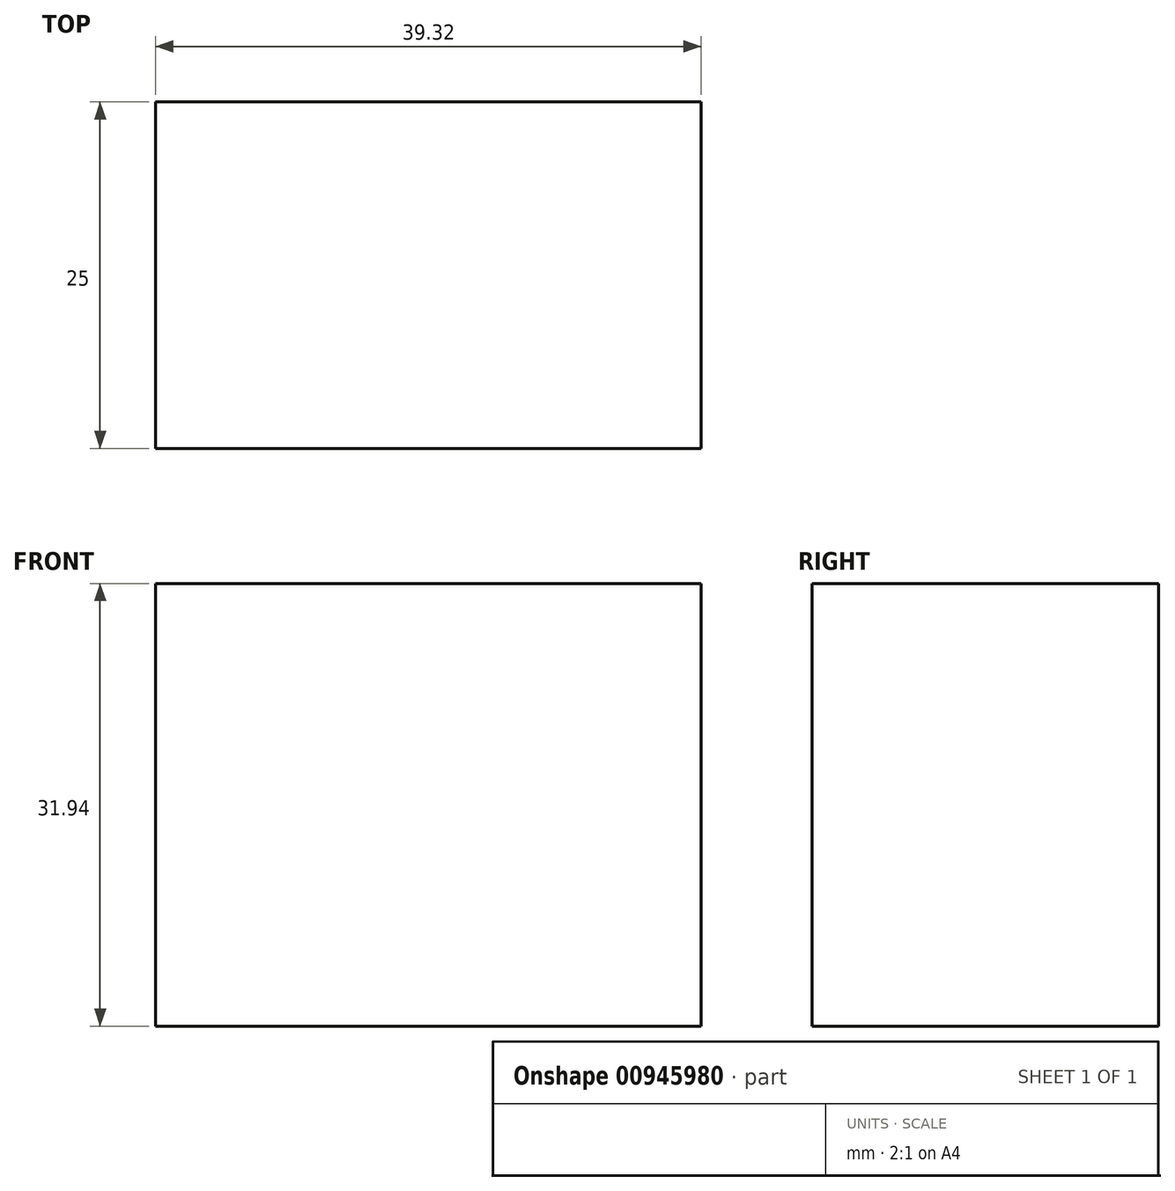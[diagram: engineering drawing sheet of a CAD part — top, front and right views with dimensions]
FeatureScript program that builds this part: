
annotation { "Feature Type Name" : "Feature", "Feature Type Description" : "" }
export const myFeature = defineFeature(function(context is Context, id is Id, definition is map)
    precondition{}
    {
        {
            var Q0;
            Q0=qCreatedBy(makeId("Front.planeOp"),FACE);
            var sketch = newSketch(context, id + "F0", { "sketchPlane" : qUnion([Q0])});
            skLineSegment(sketch, "E0.bottom", {"start": v(-41.65, 20.4) * mm, "end": v(-2.33, 20.4) * mm});
            skLineSegment(sketch, "E0.top", {"start": v(-41.65, -11.55) * mm, "end": v(-2.33, -11.55) * mm});
            skLineSegment(sketch, "E0.left", {"start": v(-41.65, 20.4) * mm, "end": v(-41.65, -11.55) * mm});
            skLineSegment(sketch, "E0.right", {"start": v(-2.33, 20.4) * mm, "end": v(-2.33, -11.55) * mm});
            skSolve(sketch);
        }
        {
            var Q0;
            Q0=makeQuery(id+"F0.imprint","IMPRINT",FACE,{"disambiguationData":[TD([[makeQuery(id+"F0.imprint","IMPRINT",EDGE,{"derivedFrom":sQuery(id+"F0.wireOp",EDGE,"E0.bottom")}),-1.0]])]});
            extrude(context, id + "F1", {"entities" : qUnion([Q0]), "depth" : 25 * mm, "offsetDistance" : 25 * mm});
        }
    });
